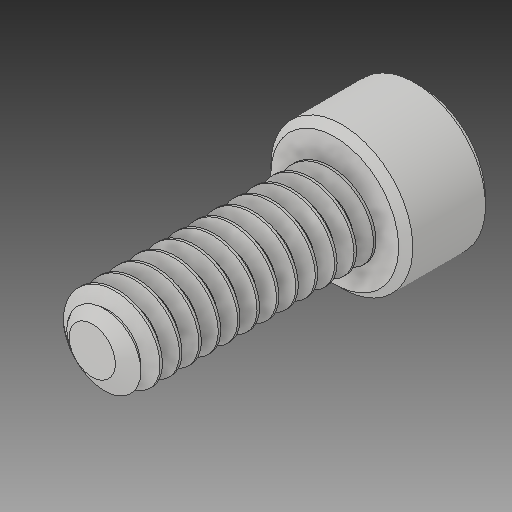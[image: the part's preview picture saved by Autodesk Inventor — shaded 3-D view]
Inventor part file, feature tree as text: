
AUTODESK INVENTOR PART (.ipt)
format: ipt  version: 2017 (Build 210142000, 142)  size: 647,168 bytes
history: native  units: in
note: dims shown in document units (in); Inventor stores cm internally (conversion verified against a paired STEP export)
features: chamfer x1
ambient origin geometry x8: Origin, YZ Plane, XZ Plane, XY Plane, X Axis, Y Axis, Z Axis, Center Point
bodies: Solid1 (feature_tree)
feature tree (1):
  chamfer  "Chamfer1"  [1 undecoded]
note: 1 required parameter value undecoded (feature->parameter linkage not recoverable at this tier; creation-order binding heuristic only, values carry confidence <= 0.55)
